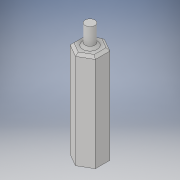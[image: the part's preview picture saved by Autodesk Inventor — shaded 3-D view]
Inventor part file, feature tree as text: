
AUTODESK INVENTOR PART (.ipt)
format: ipt  version: 2017 (Build 210142000, 142)  size: 119,296 bytes
history: native  units: in
note: dims shown in document units (in); Inventor stores cm internally (conversion verified against a paired STEP export)
features: sketch x3, extrude x1, plane x1, sweep x1, chamfer x1
ambient origin geometry x8: Origin, YZ Plane, XZ Plane, XY Plane, X Axis, Y Axis, Z Axis, Center Point
bodies: Solid1 (feature_tree)
feature tree (7):
  extrude  "Hexagon1"  Depth=5.0in TaperAngle=0.0deg
  sketch  "Sketch2"  dims[d3=0.5in d8=0.5in]
  plane  "Work Plane2"
  sweep  "Sweep1"
  chamfer  "Chamfer1"  [1 undecoded]
  sketch  "Sketch1"  dims[d0=1.5in d1=5.0in d2=0.0in]
  sketch  "Sketch5"  dims[d9=1.0in d10=0.0in d11=0.0in d12=0.125in d13=0.125in d14=45.0deg]
note: 1 required parameter value undecoded (feature->parameter linkage not recoverable at this tier; creation-order binding heuristic only, values carry confidence <= 0.55)
